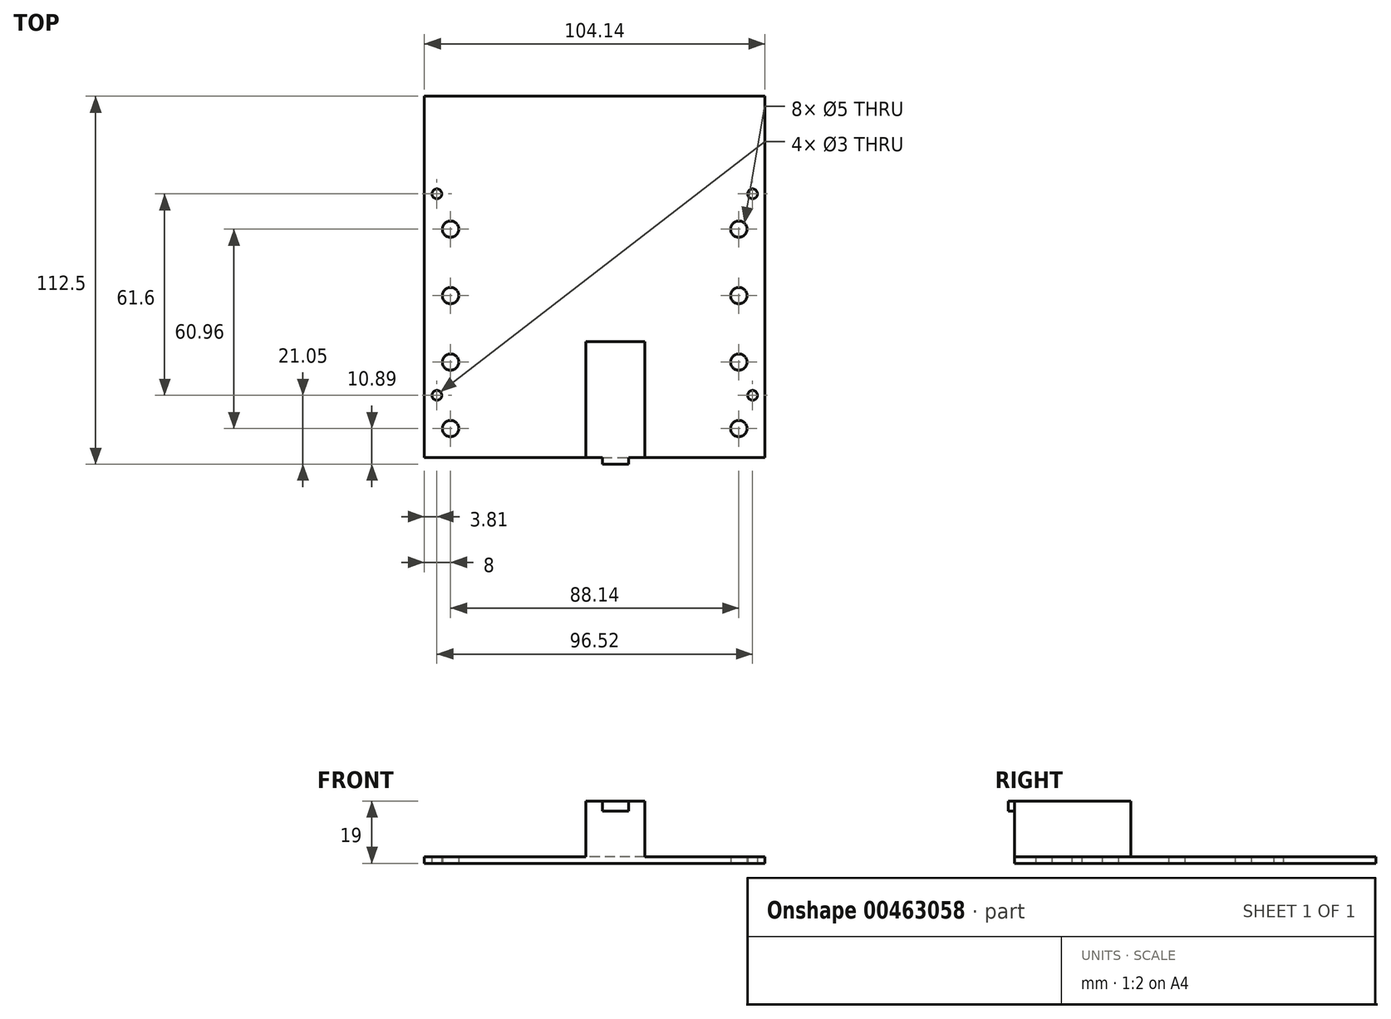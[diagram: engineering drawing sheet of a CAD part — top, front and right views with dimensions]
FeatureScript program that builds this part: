
annotation { "Feature Type Name" : "Feature", "Feature Type Description" : "" }
export const myFeature = defineFeature(function(context is Context, id is Id, definition is map)
    precondition{}
    {
        {
            var Q0;
            Q0=qCreatedBy(makeId("Top.planeOp"),FACE);
            var sketch = newSketch(context, id + "F0", { "sketchPlane" : qUnion([Q0])});
            skLineSegment(sketch, "E0.bottom", {"start": v(52.07, -55.25) * mm, "end": v(-52.07, -55.25) * mm});
            skLineSegment(sketch, "E0.top", {"start": v(52.07, 55.25) * mm, "end": v(-52.07, 55.25) * mm});
            skLineSegment(sketch, "E0.left", {"start": v(52.07, -55.25) * mm, "end": v(52.07, 55.25) * mm});
            skLineSegment(sketch, "E0.right", {"start": v(-52.07, -55.25) * mm, "end": v(-52.07, 55.25) * mm});
            skPoint(sketch, "E0.middle", {"position": v(0, 0) * mm});
            skCircle(sketch, "E1", {"center": v(-48.26, 25.4) * mm, "radius": 1.5 * mm});
            skCircle(sketch, "E2", {"center": v(48.26, -36.2) * mm, "radius": 1.5 * mm});
            skCircle(sketch, "E3", {"center": v(48.26, 25.4) * mm, "radius": 1.5 * mm});
            skCircle(sketch, "E4", {"center": v(-48.26, -36.2) * mm, "radius": 1.5 * mm});
            skCircle(sketch, "E5", {"center": v(-44.07, -46.36) * mm, "radius": 2.5 * mm});
            skCircle(sketch, "E6", {"center": v(-44.07, -26.04) * mm, "radius": 2.5 * mm});
            skCircle(sketch, "E7", {"center": v(-44.07, -5.72) * mm, "radius": 2.5 * mm});
            skCircle(sketch, "E8", {"center": v(-44.07, 14.6) * mm, "radius": 2.5 * mm});
            skCircle(sketch, "E9", {"center": v(44.07, -46.36) * mm, "radius": 2.5 * mm});
            skCircle(sketch, "E10", {"center": v(44.07, -26.04) * mm, "radius": 2.5 * mm});
            skCircle(sketch, "E11", {"center": v(44.07, -5.72) * mm, "radius": 2.5 * mm});
            skCircle(sketch, "E12", {"center": v(44.07, 14.6) * mm, "radius": 2.5 * mm});
            skSolve(sketch);
        }
        {
            var Q0;
            Q0=qSketchRegion(id+"F0",true);
            extrude(context, id + "F1", {"entities" : qUnion([Q0]), "depth" : 2 * mm});
        }
        {
            var Q0;
            Q0=makeQuery(id+"F1.opExtrude","CAP_FACE",FACE,{"disambiguationData":[OSD([sQuery(id+"F0.wireOp",EDGE,"E0.bottom"),sQuery(id+"F0.wireOp",EDGE,"E0.top"),sQuery(id+"F0.wireOp",EDGE,"E0.left"),sQuery(id+"F0.wireOp",EDGE,"E0.right"),sQuery(id+"F0.wireOp",EDGE,"E1"),sQuery(id+"F0.wireOp",EDGE,"E2"),sQuery(id+"F0.wireOp",EDGE,"E3"),sQuery(id+"F0.wireOp",EDGE,"E4")])],"isStart":false});
            cPlane(context, id + "F2", {"entities" : qUnion([Q0]), "cplaneType" : CPlaneType.OFFSET, "offset" : 0 * mm, "width" : 150 * mm, "height" : 150 * mm});
        }
        {
            var Q0;
            Q0=qCreatedBy(id+"F2.planeOp",FACE);
            var sketch = newSketch(context, id + "F3", { "sketchPlane" : qUnion([Q0])});
            skLineSegment(sketch, "E13.0", {"start": v(52.07, -55.25) * mm, "end": v(-52.07, -55.25) * mm, "construction": true});
            skLineSegment(sketch, "E14.0", {"start": v(-52.07, -55.25) * mm, "end": v(-52.07, 55.25) * mm, "construction": true});
            skLineSegment(sketch, "E15.0", {"start": v(52.07, -55.25) * mm, "end": v(52.07, 55.25) * mm, "construction": true});
            skLineSegment(sketch, "E16.bottom", {"start": v(15.35, -55.25) * mm, "end": v(-2.65, -55.25) * mm});
            skLineSegment(sketch, "E16.top", {"start": v(15.35, -19.75) * mm, "end": v(-2.65, -19.75) * mm});
            skLineSegment(sketch, "E16.left", {"start": v(15.35, -55.25) * mm, "end": v(15.35, -19.75) * mm});
            skLineSegment(sketch, "E16.right", {"start": v(-2.65, -55.25) * mm, "end": v(-2.65, -19.75) * mm});
            skLineSegment(sketch, "E17", {"start": v(6.35, 0) * mm, "end": v(6.35, -67.94) * mm, "construction": true});
            skSolve(sketch);
        }
        {
            var Q0;
            Q0=qSketchRegion(id+"F3",true);
            extrude(context, id + "F4", {"entities" : qUnion([Q0]), "operationType" : NewBodyOperationType.ADD, "depth" : 17 * mm});
        }
        {
            var Q0;
            Q0=makeQuery(id+"F1.opExtrude","SWEPT_FACE",FACE,{"disambiguationData":[OSD([sQuery(id+"F0.wireOp",EDGE,"E0.bottom")])]});
            cPlane(context, id + "F5", {"entities" : qUnion([Q0]), "cplaneType" : CPlaneType.OFFSET, "offset" : 0 * mm, "width" : 150 * mm, "height" : 150 * mm});
        }
        {
            var Q0;
            Q0=qCreatedBy(id+"F5.planeOp",FACE);
            var sketch = newSketch(context, id + "F6", { "sketchPlane" : qUnion([Q0])});
            skLineSegment(sketch, "E18.0", {"start": v(15.35, 19) * mm, "end": v(-2.65, 19) * mm, "construction": true});
            skLineSegment(sketch, "E19.0", {"start": v(52.07, 0) * mm, "end": v(-52.07, 0) * mm, "construction": true});
            skLineSegment(sketch, "E20.bottom", {"start": v(2.35, 19) * mm, "end": v(10.35, 19) * mm});
            skLineSegment(sketch, "E20.top", {"start": v(2.35, 16) * mm, "end": v(10.35, 16) * mm});
            skLineSegment(sketch, "E20.left", {"start": v(2.35, 19) * mm, "end": v(2.35, 16) * mm});
            skLineSegment(sketch, "E20.right", {"start": v(10.35, 19) * mm, "end": v(10.35, 16) * mm});
            skLineSegment(sketch, "E21", {"start": v(6.35, 19) * mm, "end": v(6.35, 5.81) * mm, "construction": true});
            skPoint(sketch, "E21.endSnap0", {"position": v(6.35, 19) * mm});
            skSolve(sketch);
        }
        {
            var Q0;
            Q0=qSketchRegion(id+"F6",true);
            extrude(context, id + "F7", {"entities" : qUnion([Q0]), "operationType" : NewBodyOperationType.ADD, "depth" : 2 * mm});
        }
    });
